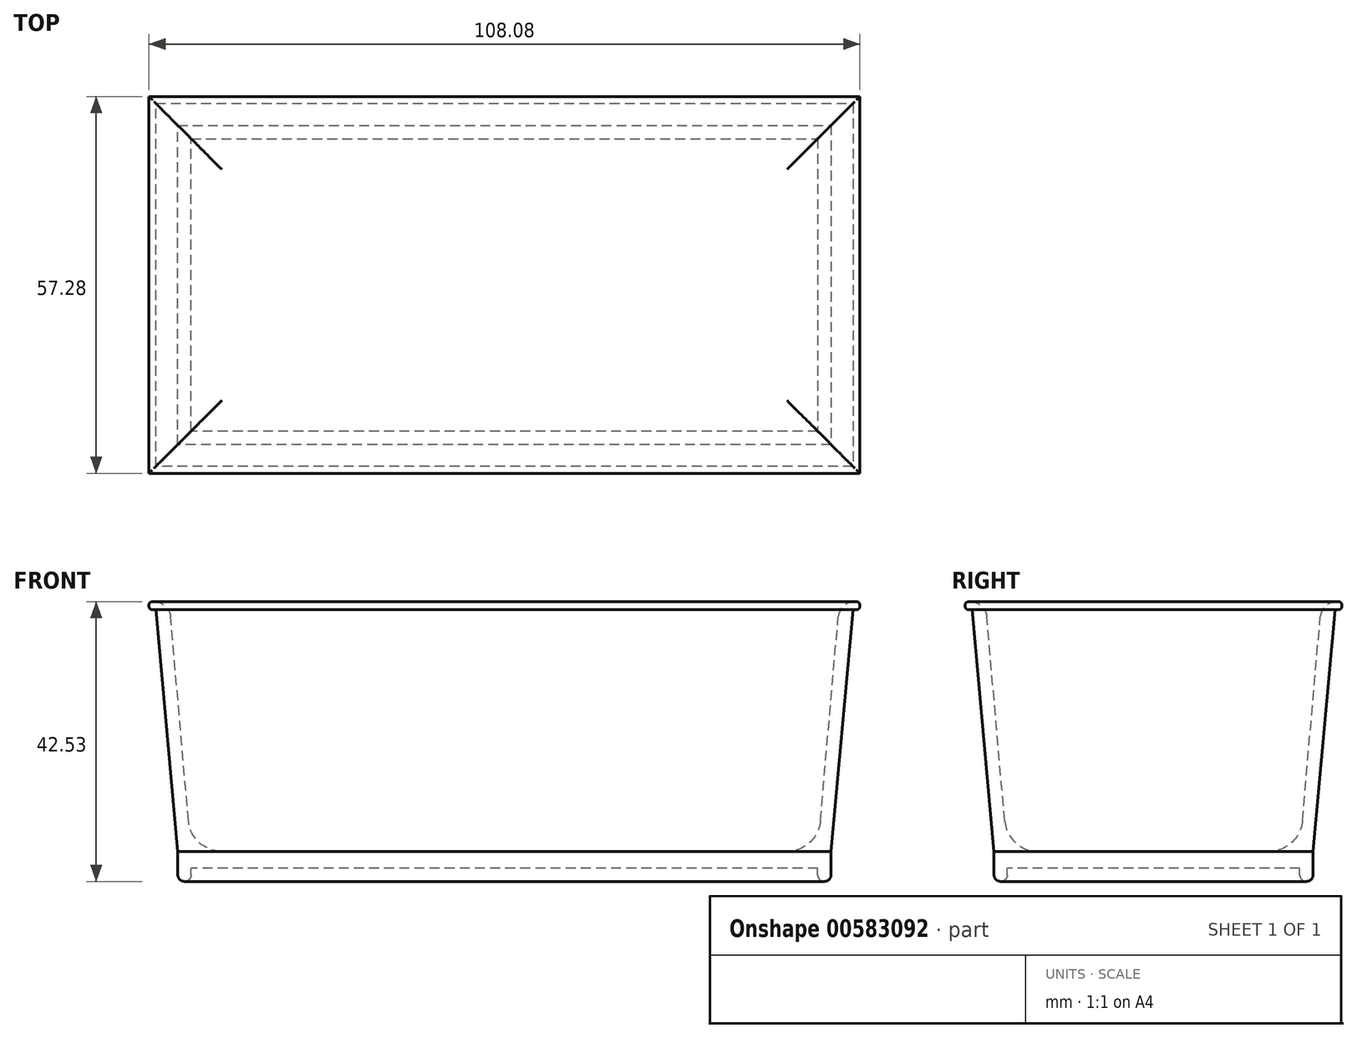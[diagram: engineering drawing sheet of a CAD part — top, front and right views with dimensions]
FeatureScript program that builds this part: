
annotation { "Feature Type Name" : "Feature", "Feature Type Description" : "" }
export const myFeature = defineFeature(function(context is Context, id is Id, definition is map)
    precondition{}
    {
        {
            var Q0;
            Q0=qCreatedBy(makeId("Top.planeOp"),FACE);
            var sketch = newSketch(context, id + "F0", { "sketchPlane" : qUnion([Q0])});
            skLineSegment(sketch, "E0.bottom", {"start": v(47.63, 22.23) * mm, "end": v(-47.63, 22.23) * mm});
            skLineSegment(sketch, "E0.top", {"start": v(47.63, -22.23) * mm, "end": v(-47.63, -22.23) * mm});
            skLineSegment(sketch, "E0.left", {"start": v(47.63, 22.23) * mm, "end": v(47.63, -22.23) * mm});
            skLineSegment(sketch, "E0.right", {"start": v(-47.63, 22.23) * mm, "end": v(-47.63, -22.23) * mm});
            skPoint(sketch, "E0.middle", {"position": v(0, 0) * mm});
            skLineSegment(sketch, "E1.0", {"start": v(50.8, 25.4) * mm, "end": v(-50.8, 25.4) * mm});
            skLineSegment(sketch, "E1.1", {"start": v(50.8, 25.4) * mm, "end": v(50.8, -25.4) * mm});
            skLineSegment(sketch, "E1.2", {"start": v(50.8, -25.4) * mm, "end": v(-50.8, -25.4) * mm});
            skLineSegment(sketch, "E1.3", {"start": v(-50.8, 25.4) * mm, "end": v(-50.8, -25.4) * mm});
            skSolve(sketch);
        }
        {
            var Q0;
            Q0=makeQuery(id+"F0.imprint","IMPRINT",FACE,{"disambiguationData":[TD([[makeQuery(id+"F0.imprint","IMPRINT",EDGE,{"derivedFrom":sQuery(id+"F0.wireOp",EDGE,"E0.bottom")}),1.0]])]});
            extrude(context, id + "F1", {"entities" : qUnion([Q0]), "depth" : 2.54 * mm, "offsetDistance" : 25.4 * mm});
        }
        {
            var Q0;
            Q0=makeQuery(id+"F1.opExtrude","SWEPT_FACE",FACE,{"disambiguationData":[OSD([sQuery(id+"F0.wireOp",EDGE,"E0.top")])]});
            var sketch = newSketch(context, id + "F2", { "sketchPlane" : qUnion([Q0])});
            skLineSegment(sketch, "E2", {"start": v(-49.66, 2.54) * mm, "end": v(-49.66, -2.03) * mm});
            skLineSegment(sketch, "E3", {"start": v(-49.66, -2.03) * mm, "end": v(-47.63, -2.03) * mm});
            skLineSegment(sketch, "E4", {"start": v(-47.63, -2.03) * mm, "end": v(-47.63, 0) * mm});
            skLineSegment(sketch, "E5", {"start": v(-47.63, 2.54) * mm, "end": v(-50.95, 40.5) * mm});
            skLineSegment(sketch, "E6", {"start": v(-50.95, 40.5) * mm, "end": v(-54.04, 40.5) * mm});
            skLineSegment(sketch, "E7", {"start": v(-54.04, 40.5) * mm, "end": v(-54.04, 39.27) * mm});
            skLineSegment(sketch, "E8", {"start": v(-54.04, 39.27) * mm, "end": v(-53, 39.27) * mm});
            skLineSegment(sketch, "E9", {"start": v(-53, 39.27) * mm, "end": v(-49.66, 2.54) * mm});
            skSolve(sketch);
        }
        {
            var Q0;
            Q0=makeQuery(id+"F2.imprint","IMPRINT",FACE,{"disambiguationData":[TD([[makeQuery(id+"F2.imprint","IMPRINT",EDGE,{"derivedFrom":sQuery(id+"F2.wireOp",EDGE,"E2")}),1.0]])]});
            var Q1;
            Q1=makeQuery(id+"F1.opExtrude","CAP_EDGE",EDGE,{"disambiguationData":[OSD([sQuery(id+"F0.wireOp",EDGE,"E0.right")])],"isStart":false});
            var Q2;
            Q2=makeQuery(id+"F1.opExtrude","CAP_EDGE",EDGE,{"disambiguationData":[OSD([sQuery(id+"F0.wireOp",EDGE,"E0.bottom")])],"isStart":false});
            var Q3;
            Q3=makeQuery(id+"F1.opExtrude","CAP_EDGE",EDGE,{"disambiguationData":[OSD([sQuery(id+"F0.wireOp",EDGE,"E0.left")])],"isStart":false});
            var Q4;
            Q4=makeQuery(id+"F1.opExtrude","CAP_EDGE",EDGE,{"disambiguationData":[OSD([sQuery(id+"F0.wireOp",EDGE,"E0.top")])],"isStart":false});
            sweep(context, id + "F3", {"operationType" : NewBodyOperationType.ADD, "profiles" : qUnion([Q0]), "path" : qUnion([Q1, Q2, Q3, Q4])});
        }
        {
            var Q0;
            Q0=makeQuery(id+"F3.opSweep","SWEPT_EDGE",EDGE,{"disambiguationData":[OSD([sQuery(id+"F0.wireOp",EDGE,"E0.right"),sQuery(id+"F2.wireOp",EDGE,"E2"),sQuery(id+"F2.wireOp",EDGE,"E3")])]});
            var Q1;
            Q1=makeQuery(id+"F3.opSweep","SWEPT_EDGE",EDGE,{"disambiguationData":[OSD([sQuery(id+"F0.wireOp",EDGE,"E0.right"),sQuery(id+"F2.wireOp",EDGE,"E3"),sQuery(id+"F2.wireOp",EDGE,"E4")])]});
            var Q2;
            Q2=makeQuery(id+"F3.opSweep","SWEPT_EDGE",EDGE,{"disambiguationData":[OSD([sQuery(id+"F0.wireOp",EDGE,"E0.top"),sQuery(id+"F2.wireOp",EDGE,"E2"),sQuery(id+"F2.wireOp",EDGE,"E3")])]});
            var Q3;
            Q3=makeQuery(id+"F3.opSweep","SWEPT_EDGE",EDGE,{"disambiguationData":[OSD([sQuery(id+"F0.wireOp",EDGE,"E0.top"),sQuery(id+"F2.wireOp",EDGE,"E3"),sQuery(id+"F2.wireOp",EDGE,"E4")])]});
            var Q4;
            Q4=makeQuery(id+"F3.opSweep","SWEPT_EDGE",EDGE,{"disambiguationData":[OSD([sQuery(id+"F0.wireOp",EDGE,"E0.bottom"),sQuery(id+"F2.wireOp",EDGE,"E3"),sQuery(id+"F2.wireOp",EDGE,"E4")])]});
            var Q5;
            Q5=makeQuery(id+"F3.opSweep","SWEPT_EDGE",EDGE,{"disambiguationData":[OSD([sQuery(id+"F0.wireOp",EDGE,"E0.bottom"),sQuery(id+"F2.wireOp",EDGE,"E2"),sQuery(id+"F2.wireOp",EDGE,"E3")])]});
            var Q6;
            Q6=makeQuery(id+"F3.opSweep","SWEPT_EDGE",EDGE,{"disambiguationData":[OSD([sQuery(id+"F0.wireOp",EDGE,"E0.left"),sQuery(id+"F2.wireOp",EDGE,"E3"),sQuery(id+"F2.wireOp",EDGE,"E4")])]});
            var Q7;
            Q7=makeQuery(id+"F3.opSweep","SWEPT_EDGE",EDGE,{"disambiguationData":[OSD([sQuery(id+"F0.wireOp",EDGE,"E0.left"),sQuery(id+"F2.wireOp",EDGE,"E2"),sQuery(id+"F2.wireOp",EDGE,"E3")])]});
            fillet(context, id + "F4", {"entities" : qUnion([Q0, Q1, Q2, Q3, Q4, Q5, Q6, Q7]), "radius" : 1.02 * mm, "tangentPropagation" : true, "allowEdgeOverflow" : false});
        }
        {
            var Q0;
            {var subQ0=sQuery(id+"F0.wireOp",EDGE,"E0.bottom");Q0=makeQuery(id+"F3.boolean.opBoolean","MERGE",EDGE,{"derivedFrom":[makeQuery(id+"F1.opExtrude","CAP_EDGE",EDGE,{"disambiguationData":[OSD([subQ0])],"isStart":false}),makeQuery(id+"F3.opSweep","SWEPT_EDGE",EDGE,{"disambiguationData":[OSD([subQ0,sQuery(id+"F0.wireOp",EDGE,"E0.top"),sQuery(id+"F0.wireOp",EDGE,"E0.right"),sQuery(id+"F2.wireOp",EDGE,"E5")])]})]});}
            var Q1;
            {var subQ0=sQuery(id+"F2.wireOp",EDGE,"E5");var subQ1=sQuery(id+"F0.wireOp",EDGE,"E0.top");var subQ2=sQuery(id+"F0.wireOp",EDGE,"E0.right");var subQ3=makeQuery(id+"F1.opExtrude","CAP_EDGE",EDGE,{"disambiguationData":[OSD([subQ2])],"isStart":false});Q1=makeQuery(id+"F3.boolean.opBoolean","MERGE",EDGE,{"derivedFrom":[subQ3,makeQuery(id+"F3.opSweep","SWEPT_EDGE",EDGE,{"disambiguationData":[OSD([subQ1,subQ2,subQ0]),TDD([subQ3,makeQuery(id+"F2.imprint","INTERSECT",VERTEX,{"derivedFrom":[makeQuery(id+"F1.opExtrude","SWEPT_EDGE",EDGE,{"disambiguationData":[OSD([subQ1,subQ2])]}),makeQuery(id+"F1.opExtrude","CAP_EDGE",EDGE,{"disambiguationData":[OSD([subQ1])],"isStart":false}),subQ0]})])]})]});}
            var Q2;
            {var subQ0=sQuery(id+"F0.wireOp",EDGE,"E0.left");Q2=makeQuery(id+"F3.boolean.opBoolean","MERGE",EDGE,{"derivedFrom":[makeQuery(id+"F1.opExtrude","CAP_EDGE",EDGE,{"disambiguationData":[OSD([subQ0])],"isStart":false}),makeQuery(id+"F3.opSweep","SWEPT_EDGE",EDGE,{"disambiguationData":[OSD([sQuery(id+"F0.wireOp",EDGE,"E0.top"),subQ0,sQuery(id+"F0.wireOp",EDGE,"E0.right"),sQuery(id+"F2.wireOp",EDGE,"E5")])]})]});}
            var Q3;
            {var subQ0=sQuery(id+"F2.wireOp",EDGE,"E5");var subQ1=sQuery(id+"F0.wireOp",EDGE,"E0.top");var subQ2=makeQuery(id+"F1.opExtrude","CAP_EDGE",EDGE,{"disambiguationData":[OSD([subQ1])],"isStart":false});var subQ3=sQuery(id+"F0.wireOp",EDGE,"E0.right");Q3=makeQuery(id+"F3.boolean.opBoolean","MERGE",EDGE,{"derivedFrom":[subQ2,makeQuery(id+"F3.opSweep","SWEPT_EDGE",EDGE,{"disambiguationData":[OSD([subQ1,subQ3,subQ0]),TDD([subQ2,makeQuery(id+"F2.imprint","INTERSECT",VERTEX,{"derivedFrom":[makeQuery(id+"F1.opExtrude","SWEPT_EDGE",EDGE,{"disambiguationData":[OSD([subQ1,subQ3])]}),subQ2,subQ0]})])]})]});}
            fillet(context, id + "F5", {"entities" : qUnion([Q0, Q1, Q2, Q3]), "radius" : 5.08 * mm, "tangentPropagation" : true, "allowEdgeOverflow" : false});
        }
        {
            var Q0;
            Q0=makeQuery(id+"F3.opSweep","SWEPT_EDGE",EDGE,{"disambiguationData":[OSD([sQuery(id+"F0.wireOp",EDGE,"E0.left"),sQuery(id+"F2.wireOp",EDGE,"E5"),sQuery(id+"F2.wireOp",EDGE,"E6")])]});
            var Q1;
            Q1=makeQuery(id+"F3.opSweep","SWEPT_EDGE",EDGE,{"disambiguationData":[OSD([sQuery(id+"F0.wireOp",EDGE,"E0.top"),sQuery(id+"F2.wireOp",EDGE,"E5"),sQuery(id+"F2.wireOp",EDGE,"E6")])]});
            var Q2;
            Q2=makeQuery(id+"F3.opSweep","SWEPT_EDGE",EDGE,{"disambiguationData":[OSD([sQuery(id+"F0.wireOp",EDGE,"E0.right"),sQuery(id+"F2.wireOp",EDGE,"E5"),sQuery(id+"F2.wireOp",EDGE,"E6")])]});
            var Q3;
            Q3=makeQuery(id+"F3.opSweep","SWEPT_EDGE",EDGE,{"disambiguationData":[OSD([sQuery(id+"F0.wireOp",EDGE,"E0.bottom"),sQuery(id+"F2.wireOp",EDGE,"E5"),sQuery(id+"F2.wireOp",EDGE,"E6")])]});
            fillet(context, id + "F6", {"entities" : qUnion([Q0, Q1, Q2, Q3]), "radius" : 2.54 * mm, "tangentPropagation" : true, "allowEdgeOverflow" : false});
        }
        {
            var Q0;
            Q0=makeQuery(id+"F3.opSweep","SWEPT_EDGE",EDGE,{"disambiguationData":[OSD([sQuery(id+"F0.wireOp",EDGE,"E0.bottom"),sQuery(id+"F2.wireOp",EDGE,"E7"),sQuery(id+"F2.wireOp",EDGE,"E8")])]});
            var Q1;
            Q1=makeQuery(id+"F3.opSweep","SWEPT_EDGE",EDGE,{"disambiguationData":[OSD([sQuery(id+"F0.wireOp",EDGE,"E0.bottom"),sQuery(id+"F2.wireOp",EDGE,"E6"),sQuery(id+"F2.wireOp",EDGE,"E7")])]});
            var Q2;
            Q2=makeQuery(id+"F3.opSweep","SWEPT_EDGE",EDGE,{"disambiguationData":[OSD([sQuery(id+"F0.wireOp",EDGE,"E0.right"),sQuery(id+"F2.wireOp",EDGE,"E6"),sQuery(id+"F2.wireOp",EDGE,"E7")])]});
            var Q3;
            Q3=makeQuery(id+"F3.opSweep","SWEPT_EDGE",EDGE,{"disambiguationData":[OSD([sQuery(id+"F0.wireOp",EDGE,"E0.right"),sQuery(id+"F2.wireOp",EDGE,"E7"),sQuery(id+"F2.wireOp",EDGE,"E8")])]});
            var Q4;
            Q4=makeQuery(id+"F3.opSweep","SWEPT_EDGE",EDGE,{"disambiguationData":[OSD([sQuery(id+"F0.wireOp",EDGE,"E0.top"),sQuery(id+"F2.wireOp",EDGE,"E6"),sQuery(id+"F2.wireOp",EDGE,"E7")])]});
            var Q5;
            Q5=makeQuery(id+"F3.opSweep","SWEPT_EDGE",EDGE,{"disambiguationData":[OSD([sQuery(id+"F0.wireOp",EDGE,"E0.top"),sQuery(id+"F2.wireOp",EDGE,"E7"),sQuery(id+"F2.wireOp",EDGE,"E8")])]});
            var Q6;
            Q6=makeQuery(id+"F3.opSweep","SWEPT_EDGE",EDGE,{"disambiguationData":[OSD([sQuery(id+"F0.wireOp",EDGE,"E0.left"),sQuery(id+"F2.wireOp",EDGE,"E7"),sQuery(id+"F2.wireOp",EDGE,"E8")])]});
            var Q7;
            Q7=makeQuery(id+"F3.opSweep","SWEPT_EDGE",EDGE,{"disambiguationData":[OSD([sQuery(id+"F0.wireOp",EDGE,"E0.left"),sQuery(id+"F2.wireOp",EDGE,"E6"),sQuery(id+"F2.wireOp",EDGE,"E7")])]});
            fillet(context, id + "F7", {"entities" : qUnion([Q0, Q1, Q2, Q3, Q4, Q5, Q6, Q7]), "radius" : 0.5 * mm, "tangentPropagation" : true, "allowEdgeOverflow" : false});
        }
    });
